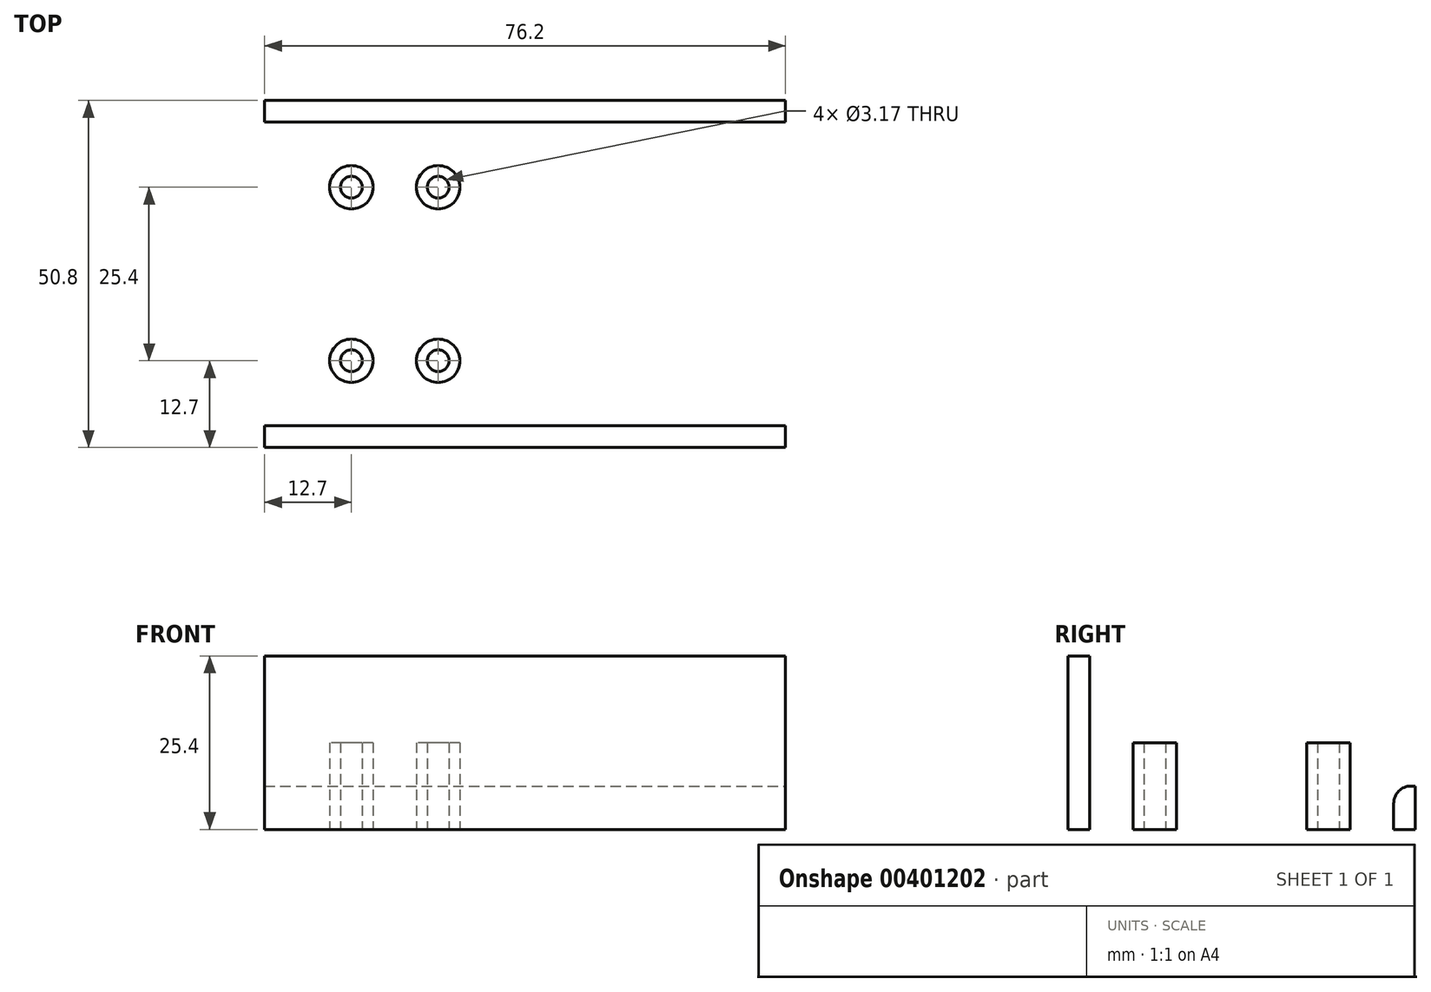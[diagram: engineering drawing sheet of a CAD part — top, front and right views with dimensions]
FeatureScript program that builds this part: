
annotation { "Feature Type Name" : "Feature", "Feature Type Description" : "" }
export const myFeature = defineFeature(function(context is Context, id is Id, definition is map)
    precondition{}
    {
        {
            var Q0;
            Q0=qCreatedBy(makeId("Top.planeOp"),FACE);
            var sketch = newSketch(context, id + "F0", { "sketchPlane" : qUnion([Q0])});
            skLineSegment(sketch, "E0.bottom", {"start": v(0, 0) * mm, "end": v(76.2, 0) * mm});
            skLineSegment(sketch, "E0.top", {"start": v(0, 50.8) * mm, "end": v(76.2, 50.8) * mm});
            skLineSegment(sketch, "E0.left", {"start": v(0, 0) * mm, "end": v(0, 50.8) * mm});
            skLineSegment(sketch, "E0.right", {"start": v(76.2, 0) * mm, "end": v(76.2, 50.8) * mm});
            skCircle(sketch, "E1", {"center": v(12.7, 38.1) * mm, "radius": 3.18 * mm});
            skCircle(sketch, "E2", {"center": v(12.7, 38.1) * mm, "radius": 1.59 * mm});
            skCircle(sketch, "E3", {"center": v(12.7, 12.7) * mm, "radius": 3.18 * mm});
            skCircle(sketch, "E4", {"center": v(12.7, 12.7) * mm, "radius": 1.59 * mm});
            skCircle(sketch, "E5", {"center": v(25.4, 38.1) * mm, "radius": 3.18 * mm});
            skCircle(sketch, "E6", {"center": v(25.4, 38.1) * mm, "radius": 1.59 * mm});
            skCircle(sketch, "E7", {"center": v(25.4, 12.7) * mm, "radius": 3.18 * mm});
            skCircle(sketch, "E8", {"center": v(25.4, 12.7) * mm, "radius": 1.59 * mm});
            skLineSegment(sketch, "E9.bottom", {"start": v(0, 3.18) * mm, "end": v(76.2, 3.18) * mm});
            skLineSegment(sketch, "E9.left", {"start": v(0, 3.18) * mm, "end": v(0, 0) * mm});
            skLineSegment(sketch, "E9.right", {"start": v(76.2, 3.18) * mm, "end": v(76.2, 0) * mm});
            skLineSegment(sketch, "E10.bottom", {"start": v(76.2, 50.8) * mm, "end": v(0, 50.8) * mm});
            skLineSegment(sketch, "E10.top", {"start": v(76.2, 47.62) * mm, "end": v(0, 47.62) * mm});
            skLineSegment(sketch, "E10.left", {"start": v(76.2, 50.8) * mm, "end": v(76.2, 47.62) * mm});
            skLineSegment(sketch, "E10.right", {"start": v(0, 50.8) * mm, "end": v(0, 47.62) * mm});
            skLineSegment(sketch, "E11.bottom", {"start": v(38.1, 25.3) * mm, "end": v(44.45, 25.3) * mm});
            skLineSegment(sketch, "E11.top", {"start": v(38.1, 24.2) * mm, "end": v(44.45, 24.2) * mm});
            skLineSegment(sketch, "E11.left", {"start": v(38.1, 25.3) * mm, "end": v(38.1, 24.2) * mm});
            skLineSegment(sketch, "E11.right", {"start": v(44.45, 25.3) * mm, "end": v(44.45, 24.2) * mm});
            skLineSegment(sketch, "E12.bottom", {"start": v(38.1, 17.84) * mm, "end": v(44.45, 17.84) * mm});
            skLineSegment(sketch, "E12.top", {"start": v(38.1, 16.73) * mm, "end": v(44.45, 16.73) * mm});
            skLineSegment(sketch, "E12.left", {"start": v(38.1, 17.84) * mm, "end": v(38.1, 16.73) * mm});
            skLineSegment(sketch, "E12.right", {"start": v(44.45, 17.84) * mm, "end": v(44.45, 16.73) * mm});
            skSolve(sketch);
        }
        {
            var Q0;
            Q0=makeQuery(id+"F0.imprint","IMPRINT",FACE,{"disambiguationData":[TD([[makeQuery(id+"F0.imprint","IMPRINT",EDGE,{"derivedFrom":sQuery(id+"F0.wireOp",EDGE,"E1")}),1.0]])]});
            var Q1;
            Q1=makeQuery(id+"F0.imprint","IMPRINT",FACE,{"disambiguationData":[TD([[makeQuery(id+"F0.imprint","IMPRINT",EDGE,{"derivedFrom":sQuery(id+"F0.wireOp",EDGE,"E3")}),1.0]])]});
            var Q2;
            Q2=makeQuery(id+"F0.imprint","IMPRINT",FACE,{"disambiguationData":[TD([[makeQuery(id+"F0.imprint","IMPRINT",EDGE,{"derivedFrom":sQuery(id+"F0.wireOp",EDGE,"E5")}),1.0]])]});
            var Q3;
            Q3=makeQuery(id+"F0.imprint","IMPRINT",FACE,{"disambiguationData":[TD([[makeQuery(id+"F0.imprint","IMPRINT",EDGE,{"derivedFrom":sQuery(id+"F0.wireOp",EDGE,"E7")}),1.0]])]});
            var Q4;
            Q4=sQuery(id+"F0.wireOp",EDGE,"E2");
            var Q5;
            Q5=sQuery(id+"F0.wireOp",EDGE,"E1");
            extrude(context, id + "F1", {"entities" : qUnion([Q0, Q1, Q2, Q3]), "surfaceEntities" : qUnion([Q4, Q5]), "depth" : 12.7 * mm});
        }
        {
            var Q0;
            Q0=makeQuery(id+"F0.imprint","IMPRINT",FACE,{"disambiguationData":[TD([[makeQuery(id+"F0.imprint","IMPRINT",EDGE,{"derivedFrom":sQuery(id+"F0.wireOp",EDGE,"E0.left")}),-1.0]])]});
            extrude(context, id + "F2", {"entities" : qUnion([Q0]), "depth" : 6.35 * mm});
        }
        {
            var Q0;
            Q0=makeQuery(id+"F0.imprint","IMPRINT",FACE,{"disambiguationData":[TD([[makeQuery(id+"F0.imprint","IMPRINT",EDGE,{"derivedFrom":sQuery(id+"F0.wireOp",EDGE,"E10.bottom")}),1.0]])]});
            var Q1;
            Q1=makeQuery(id+"F0.imprint","IMPRINT",FACE,{"disambiguationData":[TD([[makeQuery(id+"F0.imprint","IMPRINT",EDGE,{"derivedFrom":sQuery(id+"F0.wireOp",EDGE,"E9.bottom")}),-1.0]])]});
            extrude(context, id + "F3", {"entities" : qUnion([Q0, Q1]), "operationType" : NewBodyOperationType.ADD, "depth" : 25.4 * mm});
        }
        {
            var Q0;
            Q0=makeQuery(id+"F2.opExtrude","CAP_EDGE",EDGE,{"disambiguationData":[OSD([sQuery(id+"F0.wireOp",EDGE,"E10.top")])],"isStart":false});
            var Q1;
            Q1=makeQuery(id+"F2.opExtrude","CAP_EDGE",EDGE,{"disambiguationData":[OSD([sQuery(id+"F0.wireOp",EDGE,"E9.bottom")])],"isStart":false});
            fillet(context, id + "F4", {"entities" : qUnion([Q0, Q1]), "radius" : 2.54 * mm, "tangentPropagation" : true, "allowEdgeOverflow" : false});
        }
    });
